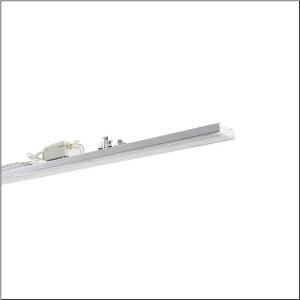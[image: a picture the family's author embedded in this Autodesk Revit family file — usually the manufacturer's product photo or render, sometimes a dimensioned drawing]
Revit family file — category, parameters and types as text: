
# Revit family: licross_11_recessed_mo_51tl12mn44xg
name_source: partatom
category: Lighting Fixtures
units: mm (PartAtom-declared; Revit-internal decimal feet)

## family parameters
Cut with Voids When Loaded = No
Host = Face
Light Source = No
Part Type = Normal
Room Calculation Point = No
Round Connector Dimension = Use Diameter
Shared = No

## types (1)
- Licross 11 Recessed MO (1 x LED, 4300 lm, 21.9 W, 4000K)
    Apparent Load = 22 VA
    CIE Flux Codes = 67 92 99 100 100
    Color Rendering = 80
    Color Temperature = 4000K
    Default Elevation = 1800 mm
    Description = Licross 11 Recessed MO, luminaire insert, of sheet steel, coil coated, white, length: 1.500mm, width: 66mm, height: 67mm, LED rated luminous flux: 4.300lm, light colour: 840, SDCM (Standard Deviation of Colour Matching)MacAdam ≤ 2 SDCM (initial), control gear: ON/OFF, with plug, 3-pole, with phase selection, mains connection: 220..240V, AC, 50/60Hz, rated input power: 22W, internal wiring halogen-free, primary optical cover: cover, of PMMA, light emission: direct distribution, primary light characteristic: symmetric, protection rating (complete): IP40, insulation class (complete): insulation class I (protective earthing), certification: CE, ENEC, VDE, UKCA, protection symbol: D if used in an environment without relevant dust loads with corresponding accessories, impact resistance: IK06, permissible ambient temperature for indoor applications: -35..+55°C, corresponds to IFS (International Featured Standards) requirements for safety and quality in the food industry, reducing of maximum allowable ambient temperature of 5°C with ceiling mounting, The light source and the operating device comply with the requirements of the Ecodesign Regulation (EU) 2019/2020 and are replaceable in accordance with this regulation, packaging unit: 1 piece
    Height = 58 mm
    Lamp = 1 x LED
    Lamp Light Flux = 4300 lm
    Lamp Power = 21.9 W
    Lamp count = 1
    Length = 1500 mm
    Luminous efficacy = 196 lm/W
    Manufacturer = Siteco
    ModVariant = No
    Model = 51TL12MN44XG
    Mounting Place = Ceiling
    Mounting Type = Pendant
    Number of Poles = 1
    OnlyDefault = Yes
    Power Factor = 1
    Product Name = Licross 11 Recessed MO
    Product group = luminaire insert | ceiling pendant
    ProductGroupID = 901
    Protection Class = Protection class I
    Protection Degree = IP 40
    RLX_Detail_Level = 1
    RLX_Emergency_Light_Flux = 0 lm
    RLX_Emergency_Type = 0
    RLX_Emergency_Type_DB = No
    RlxData = <blob elided: 21009 chars, md5=2d92385d>
    Socket = socket
    Standby Power = 0 W
    System Light Flux = 4300 lm
    System Power = 22 W
    Type Comments = Product without accessories
    Type Image = l_1296930.jpg
    URL = http://relux.com
    VarID = ---
    Voltage = 0 V
    Weight = 0.00 kg
    Width = 66 mm

## geometry (parser evidence)
native form markers: Blend x4, Sweep x11
no freeform markers — native parametric forms only
